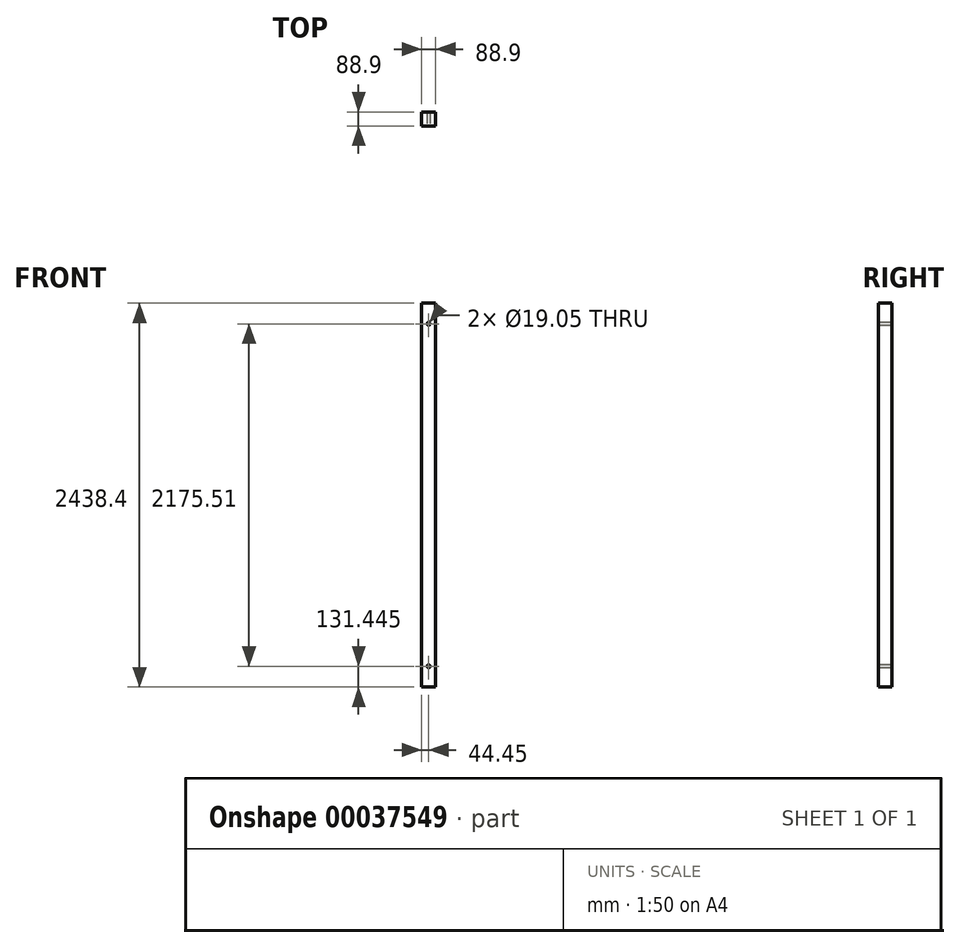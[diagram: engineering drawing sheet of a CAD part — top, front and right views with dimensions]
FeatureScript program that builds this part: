
annotation { "Feature Type Name" : "Feature", "Feature Type Description" : "" }
export const myFeature = defineFeature(function(context is Context, id is Id, definition is map)
    precondition{}
    {
        {
            var Q0;
            Q0=qCreatedBy(makeId("Top.planeOp"),FACE);
            var sketch = newSketch(context, id + "F0", { "sketchPlane" : qUnion([Q0])});
            skLineSegment(sketch, "E0.bottom", {"start": v(-44.45, 44.45) * mm, "end": v(44.45, 44.45) * mm});
            skLineSegment(sketch, "E0.top", {"start": v(-44.45, -44.45) * mm, "end": v(44.45, -44.45) * mm});
            skLineSegment(sketch, "E0.left", {"start": v(-44.45, 44.45) * mm, "end": v(-44.45, -44.45) * mm});
            skLineSegment(sketch, "E0.right", {"start": v(44.45, 44.45) * mm, "end": v(44.45, -44.45) * mm});
            skLineSegment(sketch, "E1", {"start": v(0, 0) * mm, "end": v(0, 44.45) * mm, "construction": true});
            skLineSegment(sketch, "E2", {"start": v(0, 0) * mm, "end": v(-44.45, 0) * mm, "construction": true});
            skSolve(sketch);
        }
        {
            var Q0;
            Q0=makeQuery(id+"F0.imprint","IMPRINT",FACE,{"disambiguationData":[TD([[makeQuery(id+"F0.imprint","IMPRINT",EDGE,{"derivedFrom":sQuery(id+"F0.wireOp",EDGE,"E0.bottom")}),-1.0]])]});
            extrude(context, id + "F1", {"entities" : qUnion([Q0]), "depth" : 2438.4 * mm});
        }
        {
            var Q0;
            Q0=makeQuery(id+"F1.opExtrude","SWEPT_FACE",FACE,{"disambiguationData":[OSD([sQuery(id+"F0.wireOp",EDGE,"E0.top")])]});
            var sketch = newSketch(context, id + "F2", { "sketchPlane" : qUnion([Q0])});
            skLineSegment(sketch, "E3.0.0", {"start": v(-44.45, 0) * mm, "end": v(44.45, 0) * mm});
            skLineSegment(sketch, "E3.0.1", {"start": v(44.45, 0) * mm, "end": v(44.45, 2438.4) * mm});
            skLineSegment(sketch, "E3.0.2", {"start": v(44.45, 2438.4) * mm, "end": v(-44.45, 2438.4) * mm});
            skLineSegment(sketch, "E3.0.3", {"start": v(-44.45, 2438.4) * mm, "end": v(-44.45, 0) * mm});
            skPoint(sketch, "E4", {"position": v(0, 2306.96) * mm});
            skPoint(sketch, "E5", {"position": v(0, 131.44) * mm});
            skSolve(sketch);
        }
        {
            var Q0;
            Q0=sQuery(id+"F2.wireOp",VERTEX,"E5");
            var Q1;
            Q1=sQuery(id+"F2.wireOp",VERTEX,"E4");
            var Q2;
            Q2=makeQuery(id+"F1.opExtrude","SWEPT_BODY",BODY,{"disambiguationData":[OSD([sQuery(id+"F0.wireOp",EDGE,"E0.bottom"),sQuery(id+"F0.wireOp",EDGE,"E0.top"),sQuery(id+"F0.wireOp",EDGE,"E0.left"),sQuery(id+"F0.wireOp",EDGE,"E0.right")])]});
            hole(context, id + "F3", {"style" : HoleStyle.SIMPLE, "holeDiameter" : 19.05 * mm, "endStyle" : HoleEndStyle.THROUGH, "locations" : qUnion([Q0, Q1]), "scope" : qUnion([Q2])});
        }
    });
